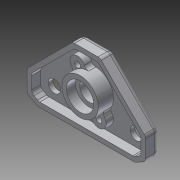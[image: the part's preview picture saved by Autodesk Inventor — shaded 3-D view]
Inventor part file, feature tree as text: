
AUTODESK INVENTOR PART (.ipt)
format: ipt  version: 2014 SP1 (Build 180222100, 222)  size: 178,688 bytes
history: native  units: in
note: dims shown in document units (in); Inventor stores cm internally (conversion verified against a paired STEP export)
features: fillet x1, other x1, imported_body x1
ambient origin geometry x8: Origin, YZ Plane, XZ Plane, XY Plane, X Axis, Y Axis, Z Axis, Center Point
bodies: Body1 (feature_tree)
feature tree (3):
  fillet  "Fillet2"  [1 undecoded]
  other  "217-2428-018 Rev2.ipt1"
  imported_body  "Base1"
note: 1 required parameter value undecoded (feature->parameter linkage not recoverable at this tier; creation-order binding heuristic only, values carry confidence <= 0.55)
